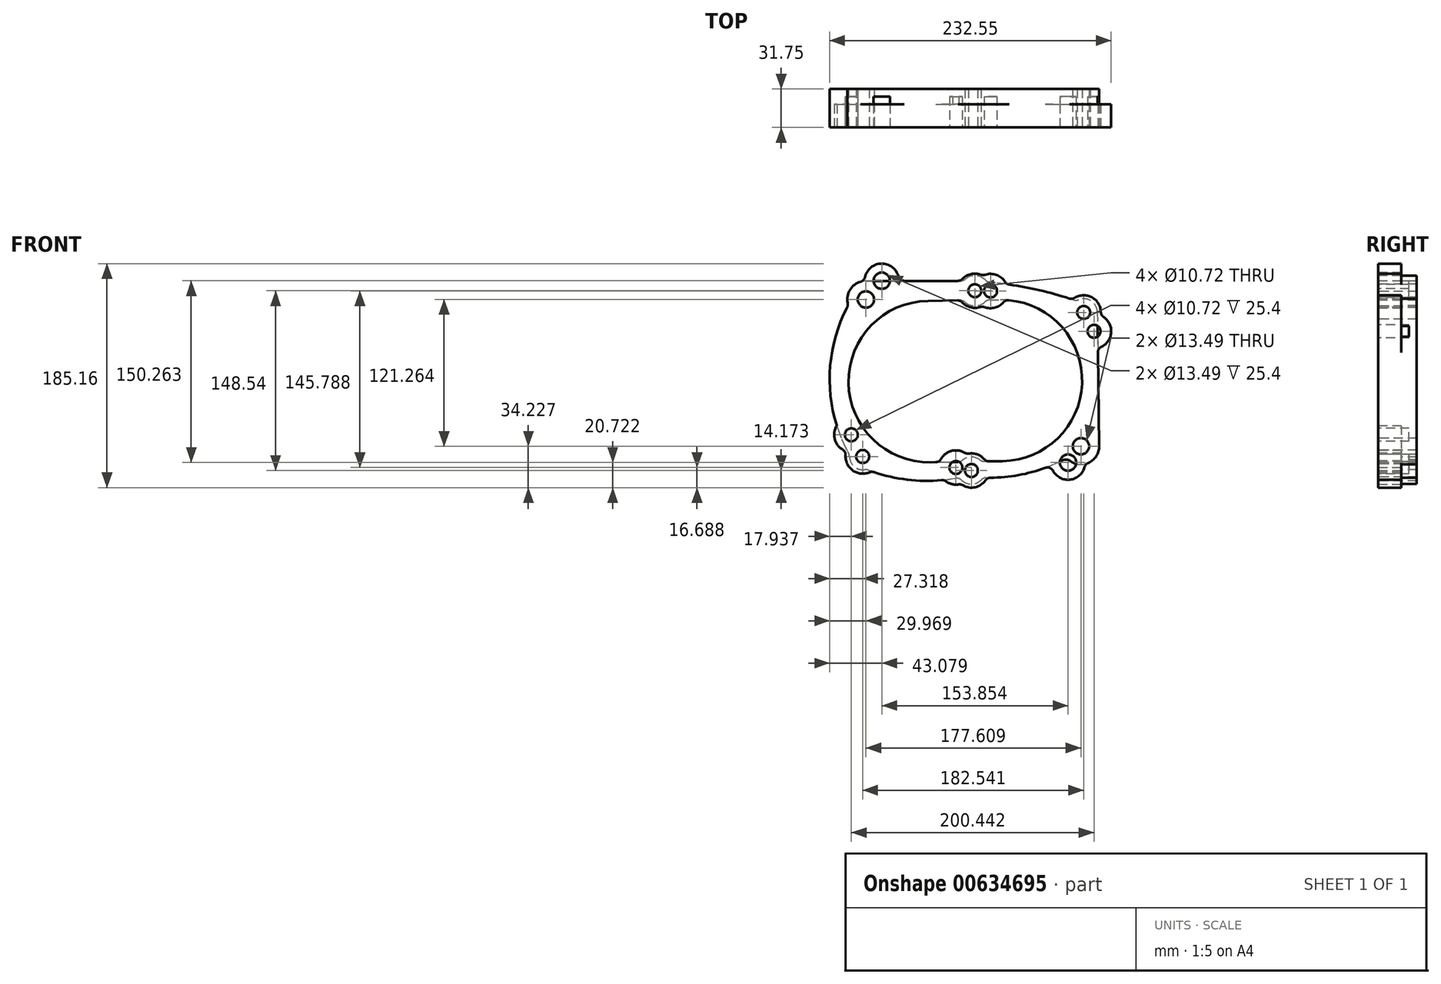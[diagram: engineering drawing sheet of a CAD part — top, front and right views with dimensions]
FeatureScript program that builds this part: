
annotation { "Feature Type Name" : "Feature", "Feature Type Description" : "" }
export const myFeature = defineFeature(function(context is Context, id is Id, definition is map)
    precondition{}
    {
        {
            var Q0;
            Q0=qCreatedBy(makeId("Front.planeOp"),FACE);
            var sketch = newSketch(context, id + "F0", { "sketchPlane" : qUnion([Q0])});
            skArc(sketch, "E0", {"start": v(18.49, 23.08) * mm, "mid": v(16.62, 24.35) * mm, "end": v(14.67, 25.49) * mm});
            skCircle(sketch, "E1", {"center": v(-15.7, 35.72) * mm, "radius": 1.38 * mm});
            skCircle(sketch, "E2", {"center": v(13.85, 35.93) * mm, "radius": 1.35 * mm});
            skCircle(sketch, "E3", {"center": v(20.07, 25.22) * mm, "radius": 1.06 * mm});
            skCircle(sketch, "E4", {"center": v(36, 22.94) * mm, "radius": 0.96 * mm});
            skCircle(sketch, "E5", {"center": v(32.47, 7.28) * mm, "radius": 1.06 * mm});
            skCircle(sketch, "E6", {"center": v(32.89, -9.33) * mm, "radius": 1.43 * mm});
            skCircle(sketch, "E7", {"center": v(29.86, -17.53) * mm, "radius": 1.14 * mm});
            skCircle(sketch, "E8", {"center": v(17.06, -30.92) * mm, "radius": 1 * mm});
            skCircle(sketch, "E9", {"center": v(-3.49, -35.34) * mm, "radius": 0.93 * mm});
            skCircle(sketch, "E10", {"center": v(-24.93, -24.43) * mm, "radius": 0.8 * mm});
            skCircle(sketch, "E11", {"center": v(-31.45, -13.73) * mm, "radius": 1.54 * mm});
            skCircle(sketch, "E12", {"center": v(-30.11, 13.1) * mm, "radius": 0.49 * mm});
            skArc(sketch, "E13", {"start": v(-33.12, -16.68) * mm, "mid": v(2.53, -38.1) * mm, "end": v(34.93, -12.05) * mm});
            skLineSegment(sketch, "E14", {"start": v(-10.28, -36.7) * mm, "end": v(-10.28, -31.1) * mm, "construction": true});
            skLineSegment(sketch, "E15", {"start": v(-6.15, -37.66) * mm, "end": v(-6.15, -32.24) * mm, "construction": true});
            skLineSegment(sketch, "E16", {"start": v(7.8, -37.36) * mm, "end": v(7.8, -31.88) * mm, "construction": true});
            skLineSegment(sketch, "E17", {"start": v(11.69, -36.28) * mm, "end": v(11.69, -30.6) * mm, "construction": true});
            skCircle(sketch, "E18", {"center": v(0.06, -1.86) * mm, "radius": 33.67 * mm, "construction": true});
            skLineSegment(sketch, "E19", {"start": v(0.06, 31.81) * mm, "end": v(0.06, 34.48) * mm, "construction": true});
            skLineSegment(sketch, "E20", {"start": v(0.06, 31.81) * mm, "end": v(0.06, 29.15) * mm, "construction": true});
            skArc(sketch, "E21", {"start": v(-34.65, -12.61) * mm, "mid": v(-34.62, -14.93) * mm, "end": v(-33.12, -16.68) * mm});
            skArc(sketch, "E22.trimOffspring", {"start": v(35.9, -7.76) * mm, "mid": v(36.4, -1.66) * mm, "end": v(35.84, 4.45) * mm});
            skArc(sketch, "E23.trimOffspring", {"start": v(34.93, -12.05) * mm, "mid": v(36.4, -10.13) * mm, "end": v(35.9, -7.76) * mm});
            skLineSegment(sketch, "E24", {"start": v(-18.74, 29.24) * mm, "end": v(-18.74, 35.72) * mm});
            skLineSegment(sketch, "E25", {"start": v(-15.7, 38.77) * mm, "end": v(13.85, 38.77) * mm});
            skLineSegment(sketch, "E26", {"start": v(16.69, 35.93) * mm, "end": v(16.69, 31.66) * mm});
            skArc(sketch, "E27.trimOffspring", {"start": v(-18.74, 29.24) * mm, "mid": v(-33.9, 11.05) * mm, "end": v(-34.65, -12.61) * mm});
            skArc(sketch, "E28", {"start": v(16.69, 31.66) * mm, "mid": v(17.37, 29.7) * mm, "end": v(19.11, 28.57) * mm});
            skArc(sketch, "E29", {"start": v(38.4, 22.45) * mm, "mid": v(37.98, 24.39) * mm, "end": v(36.27, 25.38) * mm});
            skArc(sketch, "E30", {"start": v(18.49, 23.08) * mm, "mid": v(20.67, 22.62) * mm, "end": v(22.44, 24) * mm});
            skArc(sketch, "E31", {"start": v(32.84, 9.91) * mm, "mid": v(30.46, 9.03) * mm, "end": v(29.9, 6.55) * mm});
            skLineSegment(sketch, "E32", {"start": v(19.11, 28.57) * mm, "end": v(36.63, 25.32) * mm});
            skLineSegment(sketch, "E33", {"start": v(38.4, 22.45) * mm, "end": v(35.84, 4.45) * mm});
            skArc(sketch, "E34", {"start": v(26.23, 26.04) * mm, "mid": v(24.02, 25.6) * mm, "end": v(22.44, 24) * mm});
            skArc(sketch, "E35.trimOffspring", {"start": v(35.67, 12.46) * mm, "mid": v(33.55, 21.05) * mm, "end": v(26.23, 26.04) * mm});
            skArc(sketch, "E36.trimOffspring", {"start": v(32.84, 9.91) * mm, "mid": v(34.73, 10.66) * mm, "end": v(35.67, 12.46) * mm});
            skArc(sketch, "E37.converted", {"start": v(-15.52, 32.68) * mm, "mid": v(-13.32, 33.82) * mm, "end": v(-12.69, 36.22) * mm});
            skArc(sketch, "E38.converted", {"start": v(11.03, 36.26) * mm, "mid": v(12.03, 33.76) * mm, "end": v(14.67, 33.22) * mm});
            skLineSegment(sketch, "E39", {"start": v(-15.52, 24.95) * mm, "end": v(-15.52, 32.68) * mm});
            skLineSegment(sketch, "E40", {"start": v(14.67, 25.49) * mm, "end": v(14.67, 33.22) * mm});
            skArc(sketch, "E41.trimOffspring", {"start": v(-15.52, 24.95) * mm, "mid": v(-11.58, -30.6) * mm, "end": v(29.9, 6.55) * mm});
            skLineSegment(sketch, "E42", {"start": v(-11.7, 37.38) * mm, "end": v(10.04, 37.38) * mm});
            skArc(sketch, "E43.trimOffspring", {"start": v(-15.7, 38.77) * mm, "mid": v(-17.85, 37.87) * mm, "end": v(-18.74, 35.72) * mm});
            skArc(sketch, "E44.trimOffspring", {"start": v(16.69, 35.93) * mm, "mid": v(15.86, 37.94) * mm, "end": v(13.85, 38.77) * mm});
            skArc(sketch, "E45", {"start": v(-11.7, 37.38) * mm, "mid": v(-12.47, 37.03) * mm, "end": v(-12.69, 36.22) * mm});
            skArc(sketch, "E46", {"start": v(11.03, 36.26) * mm, "mid": v(10.79, 37.04) * mm, "end": v(10.04, 37.38) * mm});
            skSolve(sketch);
        }
        {
            var Q0;
            Q0=qCreatedBy(makeId("Front.planeOp"),FACE);
            var sketch = newSketch(context, id + "F1", { "sketchPlane" : qUnion([Q0])});
            skCircle(sketch, "E47", {"center": v(145.83, 46.91) * mm, "radius": 5.36 * mm});
            skCircle(sketch, "E48", {"center": v(143.55, -63.66) * mm, "radius": 6.75 * mm});
            skCircle(sketch, "E49", {"center": v(53.04, -83.72) * mm, "radius": 5.36 * mm});
            skCircle(sketch, "E50", {"center": v(-36.71, -72.14) * mm, "radius": 5.36 * mm});
            skCircle(sketch, "E51", {"center": v(-34.06, 57.6) * mm, "radius": 6.75 * mm});
            skCircle(sketch, "E52", {"center": v(55.9, 64.82) * mm, "radius": 5.36 * mm});
            skSolve(sketch);
        }
        {
            var Q0;
            Q0=qCreatedBy(makeId("Front.planeOp"),FACE);
            var sketch = newSketch(context, id + "F2", { "sketchPlane" : qUnion([Q0])});
            skCircle(sketch, "E53.0", {"center": v(-34.06, 57.6) * mm, "radius": 6.75 * mm});
            skCircle(sketch, "E54.0", {"center": v(55.9, 64.82) * mm, "radius": 5.36 * mm});
            skCircle(sketch, "E55.0", {"center": v(145.83, 46.91) * mm, "radius": 5.36 * mm});
            skCircle(sketch, "E56.0", {"center": v(-36.71, -72.14) * mm, "radius": 5.36 * mm});
            skCircle(sketch, "E57.0", {"center": v(53.04, -83.72) * mm, "radius": 5.36 * mm});
            skCircle(sketch, "E58.0", {"center": v(143.55, -63.66) * mm, "radius": 6.75 * mm});
            skArc(sketch, "E59", {"start": v(-34.06, 72.97) * mm, "mid": v(-45.87, 67.43) * mm, "end": v(-49.17, 54.82) * mm});
            skArc(sketch, "E60", {"start": v(47.87, 55.34) * mm, "mid": v(56.08, 52.4) * mm, "end": v(64.2, 55.6) * mm});
            skArc(sketch, "E61", {"start": v(157.13, 47.06) * mm, "mid": v(152.12, 56.3) * mm, "end": v(141.68, 57.42) * mm});
            skArc(sketch, "E62", {"start": v(134.74, -75.88) * mm, "mid": v(150.5, -77.03) * mm, "end": v(158.61, -63.46) * mm});
            skArc(sketch, "E63", {"start": v(59.93, -74.87) * mm, "mid": v(52.87, -72.5) * mm, "end": v(45.89, -75.09) * mm});
            skArc(sketch, "E64", {"start": v(-47.62, -72.47) * mm, "mid": v(-43.8, -80.44) * mm, "end": v(-35.32, -82.97) * mm});
            skCircle(sketch, "E65", {"center": v(61.04, -9.57) * mm, "radius": 12.7 * mm});
            skLineSegment(sketch, "E66", {"start": v(61.04, -9.57) * mm, "end": v(53.04, -83.72) * mm, "construction": true});
            skLineSegment(sketch, "E67", {"start": v(55.9, 64.82) * mm, "end": v(61.04, -9.57) * mm, "construction": true});
            skLineSegment(sketch, "E68", {"start": v(-34.06, 57.6) * mm, "end": v(61.04, -9.57) * mm, "construction": true});
            skLineSegment(sketch, "E69", {"start": v(61.04, -9.57) * mm, "end": v(-36.71, -72.14) * mm, "construction": true});
            skLineSegment(sketch, "E70", {"start": v(61.04, -9.57) * mm, "end": v(145.83, 46.91) * mm, "construction": true});
            skLineSegment(sketch, "E71", {"start": v(61.04, -9.57) * mm, "end": v(143.55, -63.66) * mm, "construction": true});
            skLineSegment(sketch, "E72", {"start": v(-34.06, 72.97) * mm, "end": v(43.97, 72.97) * mm});
            skArc(sketch, "E73", {"start": v(137.34, 57.3) * mm, "mid": v(103.34, 66.54) * mm, "end": v(68.5, 71.84) * mm});
            skLineSegment(sketch, "E74", {"start": v(157.13, 47.06) * mm, "end": v(158.61, -63.46) * mm});
            skArc(sketch, "E75", {"start": v(-49.77, 50.77) * mm, "mid": v(-64.02, -9.6) * mm, "end": v(-48.39, -69.62) * mm});
            skArc(sketch, "E76", {"start": v(-32.26, -83.33) * mm, "mid": v(3.31, -91.62) * mm, "end": v(39.8, -90.16) * mm});
            skArc(sketch, "E77", {"start": v(65.67, -89.7) * mm, "mid": v(97.79, -86.34) * mm, "end": v(128.16, -75.37) * mm});
            skArc(sketch, "E78", {"start": v(78.86, -75.99) * mm, "mid": v(144.51, -8.3) * mm, "end": v(76.83, 57.35) * mm});
            skLineSegment(sketch, "E79", {"start": v(18.24, -10.22) * mm, "end": v(77.85, -9.32) * mm, "construction": true});
            skLineSegment(sketch, "E80", {"start": v(17.23, 56.44) * mm, "end": v(43.68, 56.85) * mm});
            skLineSegment(sketch, "E81", {"start": v(19.25, -76.89) * mm, "end": v(41.93, -76.55) * mm});
            skArc(sketch, "E82.trimOffspring", {"start": v(17.23, 56.44) * mm, "mid": v(-48.43, -11.23) * mm, "end": v(19.25, -76.89) * mm});
            skArc(sketch, "E83.trimOffspring", {"start": v(64.63, 73.65) * mm, "mid": v(56.46, 77.23) * mm, "end": v(48, 74.41) * mm});
            skLineSegment(sketch, "E84.trimOffspring", {"start": v(68.35, 57.22) * mm, "end": v(76.83, 57.35) * mm});
            skLineSegment(sketch, "E85.trimOffspring", {"start": v(63.93, -76.21) * mm, "end": v(78.86, -75.99) * mm});
            skArc(sketch, "E86.trimOffspring", {"start": v(45.3, -91.82) * mm, "mid": v(53.21, -94.93) * mm, "end": v(61.03, -91.59) * mm});
            skPoint(sketch, "E87.visualSharp", {"position": v(-48.67, 52.85) * mm});
            skArc(sketch, "E87.filletArc", {"start": v(-49.77, 50.77) * mm, "mid": v(-49.14, 52.74) * mm, "end": v(-49.17, 54.82) * mm});
            skPoint(sketch, "E88.visualSharp", {"position": v(-47.57, -71.1) * mm});
            skArc(sketch, "E88.filletArc", {"start": v(-47.62, -72.47) * mm, "mid": v(-47.84, -71) * mm, "end": v(-48.39, -69.62) * mm});
            skPoint(sketch, "E89.visualSharp", {"position": v(-33.91, -82.69) * mm});
            skArc(sketch, "E89.filletArc", {"start": v(-32.26, -83.33) * mm, "mid": v(-33.77, -82.96) * mm, "end": v(-35.32, -82.97) * mm});
            skPoint(sketch, "E90.visualSharp", {"position": v(43.42, -89.47) * mm});
            skArc(sketch, "E90.filletArc", {"start": v(45.3, -91.82) * mm, "mid": v(42.75, -90.33) * mm, "end": v(39.8, -90.16) * mm});
            skPoint(sketch, "E91.visualSharp", {"position": v(62.59, -89.6) * mm});
            skArc(sketch, "E91.filletArc", {"start": v(65.67, -89.7) * mm, "mid": v(63.15, -90.16) * mm, "end": v(61.03, -91.59) * mm});
            skPoint(sketch, "E92.visualSharp", {"position": v(44.46, -76.5) * mm});
            skArc(sketch, "E92.filletArc", {"start": v(41.93, -76.55) * mm, "mid": v(44.04, -76.15) * mm, "end": v(45.89, -75.09) * mm});
            skPoint(sketch, "E93.visualSharp", {"position": v(61.4, -76.25) * mm});
            skArc(sketch, "E93.filletArc", {"start": v(59.93, -74.87) * mm, "mid": v(61.82, -75.88) * mm, "end": v(63.93, -76.21) * mm});
            skPoint(sketch, "E94.visualSharp", {"position": v(132, -73.34) * mm});
            skArc(sketch, "E94.filletArc", {"start": v(134.74, -75.88) * mm, "mid": v(131.52, -74.7) * mm, "end": v(128.16, -75.37) * mm});
            skPoint(sketch, "E95.visualSharp", {"position": v(139.8, 56.47) * mm});
            skArc(sketch, "E95.filletArc", {"start": v(137.34, 57.3) * mm, "mid": v(139.52, 56.98) * mm, "end": v(141.68, 57.42) * mm});
            skPoint(sketch, "E96.visualSharp", {"position": v(65.68, 57.18) * mm});
            skArc(sketch, "E96.filletArc", {"start": v(68.35, 57.22) * mm, "mid": v(66.12, 56.78) * mm, "end": v(64.2, 55.6) * mm});
            skPoint(sketch, "E97.visualSharp", {"position": v(46.34, 56.89) * mm});
            skArc(sketch, "E97.filletArc", {"start": v(47.87, 55.34) * mm, "mid": v(45.91, 56.48) * mm, "end": v(43.68, 56.85) * mm});
            skPoint(sketch, "E98.visualSharp", {"position": v(46.52, 72.97) * mm});
            skArc(sketch, "E98.filletArc", {"start": v(43.97, 72.97) * mm, "mid": v(46.12, 73.34) * mm, "end": v(48, 74.41) * mm});
            skPoint(sketch, "E99.visualSharp", {"position": v(65.98, 72.06) * mm});
            skArc(sketch, "E99.filletArc", {"start": v(64.63, 73.65) * mm, "mid": v(66.4, 72.4) * mm, "end": v(68.5, 71.84) * mm});
            skSolve(sketch);
        }
        {
            var Q0;
            Q0=makeQuery(id+"F2.imprint","IMPRINT",FACE,{"disambiguationData":[TD([[makeQuery(id+"F2.imprint","IMPRINT",EDGE,{"derivedFrom":sQuery(id+"F2.wireOp",EDGE,"E53.0")}),-1.0]])]});
            extrude(context, id + "F3", {"entities" : qUnion([Q0]), "oppositeDirection" : true, "depth" : 12.7 * mm, "offsetDistance" : 25.4 * mm});
        }
        {
            var Q0;
            Q0=makeQuery(id+"F2.imprint","IMPRINT",FACE,{"disambiguationData":[TD([[makeQuery(id+"F2.imprint","IMPRINT",EDGE,{"derivedFrom":sQuery(id+"F2.wireOp",EDGE,"E53.0")}),-1.0]])]});
            extrude(context, id + "F4", {"entities" : qUnion([Q0]), "depth" : 19.05 * mm, "offsetDistance" : 25.4 * mm});
        }
        {
            var Q0;
            Q0=makeQuery(id+"F4.opExtrude","CAP_FACE",FACE,{"disambiguationData":[OSD([sQuery(id+"F2.wireOp",EDGE,"E53.0"),sQuery(id+"F2.wireOp",EDGE,"E54.0"),sQuery(id+"F2.wireOp",EDGE,"E55.0"),sQuery(id+"F2.wireOp",EDGE,"E56.0"),sQuery(id+"F2.wireOp",EDGE,"E57.0"),sQuery(id+"F2.wireOp",EDGE,"E58.0"),sQuery(id+"F2.wireOp",EDGE,"E59"),sQuery(id+"F2.wireOp",EDGE,"E60"),sQuery(id+"F2.wireOp",EDGE,"E61"),sQuery(id+"F2.wireOp",EDGE,"E62"),sQuery(id+"F2.wireOp",EDGE,"E63"),sQuery(id+"F2.wireOp",EDGE,"E64"),sQuery(id+"F2.wireOp",EDGE,"E72"),sQuery(id+"F2.wireOp",EDGE,"E73"),sQuery(id+"F2.wireOp",EDGE,"E74"),sQuery(id+"F2.wireOp",EDGE,"E75"),sQuery(id+"F2.wireOp",EDGE,"E76"),sQuery(id+"F2.wireOp",EDGE,"E77"),sQuery(id+"F2.wireOp",EDGE,"E78"),sQuery(id+"F2.wireOp",EDGE,"E80"),sQuery(id+"F2.wireOp",EDGE,"E81"),sQuery(id+"F2.wireOp",EDGE,"E82.trimOffspring"),sQuery(id+"F2.wireOp",EDGE,"E83.trimOffspring"),sQuery(id+"F2.wireOp",EDGE,"E84.trimOffspring"),sQuery(id+"F2.wireOp",EDGE,"E85.trimOffspring"),sQuery(id+"F2.wireOp",EDGE,"E86.trimOffspring"),sQuery(id+"F2.wireOp",EDGE,"E87.filletArc"),sQuery(id+"F2.wireOp",EDGE,"E88.filletArc"),sQuery(id+"F2.wireOp",EDGE,"E89.filletArc"),sQuery(id+"F2.wireOp",EDGE,"E90.filletArc"),sQuery(id+"F2.wireOp",EDGE,"E91.filletArc"),sQuery(id+"F2.wireOp",EDGE,"E92.filletArc"),sQuery(id+"F2.wireOp",EDGE,"E93.filletArc"),sQuery(id+"F2.wireOp",EDGE,"E94.filletArc"),sQuery(id+"F2.wireOp",EDGE,"E95.filletArc"),sQuery(id+"F2.wireOp",EDGE,"E96.filletArc"),sQuery(id+"F2.wireOp",EDGE,"E97.filletArc"),sQuery(id+"F2.wireOp",EDGE,"E98.filletArc"),sQuery(id+"F2.wireOp",EDGE,"E99.filletArc")])],"isStart":false});
            var sketch = newSketch(context, id + "F5", { "sketchPlane" : qUnion([Q0])});
            skCircle(sketch, "E100.0", {"center": v(-34.06, 57.6) * mm, "radius": 6.75 * mm});
            skCircle(sketch, "E101.0", {"center": v(55.9, 64.82) * mm, "radius": 5.36 * mm});
            skCircle(sketch, "E102.0", {"center": v(145.83, 46.91) * mm, "radius": 5.36 * mm});
            skCircle(sketch, "E103.0", {"center": v(143.55, -63.66) * mm, "radius": 6.75 * mm});
            skCircle(sketch, "E104.0", {"center": v(53.04, -83.72) * mm, "radius": 5.36 * mm});
            skCircle(sketch, "E105.0", {"center": v(-36.71, -72.14) * mm, "radius": 5.36 * mm});
            skCircle(sketch, "E106.0", {"center": v(61.04, -9.57) * mm, "radius": 12.7 * mm});
            skCircle(sketch, "E107.1.0", {"center": v(-20.95, 73.1) * mm, "radius": 6.75 * mm});
            skCircle(sketch, "E107.1.1", {"center": v(68.89, 64.59) * mm, "radius": 5.36 * mm});
            skCircle(sketch, "E107.1.2", {"center": v(154.35, 31.33) * mm, "radius": 5.36 * mm});
            skCircle(sketch, "E107.1.3", {"center": v(132.9, -77.17) * mm, "radius": 6.75 * mm});
            skCircle(sketch, "E107.1.4", {"center": v(40.3, -81.2) * mm, "radius": 5.36 * mm});
            skCircle(sketch, "E107.1.5", {"center": v(-46.1, -54.22) * mm, "radius": 5.36 * mm});
            skLineSegment(sketch, "E107.anchor1", {"start": v(61.04, -9.57) * mm, "end": v(-34.06, 57.6) * mm, "construction": true});
            skLineSegment(sketch, "E107.anchor2", {"start": v(61.04, -9.57) * mm, "end": v(-20.95, 73.1) * mm, "construction": true});
            skCircle(sketch, "E108", {"center": v(68.89, 64.59) * mm, "radius": 14.17 * mm});
            skCircle(sketch, "E109", {"center": v(154.35, 31.33) * mm, "radius": 14.17 * mm});
            skCircle(sketch, "E110", {"center": v(132.9, -77.17) * mm, "radius": 14.17 * mm});
            skCircle(sketch, "E111", {"center": v(40.3, -81.2) * mm, "radius": 14.17 * mm});
            skCircle(sketch, "E112", {"center": v(-46.1, -54.22) * mm, "radius": 14.17 * mm});
            skCircle(sketch, "E113", {"center": v(-20.95, 73.1) * mm, "radius": 14.17 * mm});
            skCircle(sketch, "E114.cCircle", {"center": v(-20.95, 73.1) * mm, "radius": 9.53 * mm, "construction": true});
            skLineSegment(sketch, "E114.0", {"start": v(-16.08, 82.96) * mm, "end": v(-9.98, 73.8) * mm, "construction": true});
            skLineSegment(sketch, "E114.1", {"start": v(-9.98, 73.8) * mm, "end": v(-14.85, 63.95) * mm, "construction": true});
            skLineSegment(sketch, "E114.2", {"start": v(-14.85, 63.95) * mm, "end": v(-25.82, 63.23) * mm, "construction": true});
            skLineSegment(sketch, "E114.3", {"start": v(-25.82, 63.23) * mm, "end": v(-31.93, 72.38) * mm, "construction": true});
            skLineSegment(sketch, "E114.4", {"start": v(-31.93, 72.38) * mm, "end": v(-27.05, 82.24) * mm, "construction": true});
            skLineSegment(sketch, "E114.5", {"start": v(-27.05, 82.24) * mm, "end": v(-16.08, 82.96) * mm, "construction": true});
            skPoint(sketch, "E114.0.midPoint", {"position": v(-13.03, 78.38) * mm});
            skLineSegment(sketch, "E115.0", {"start": v(-27.22, 82.49) * mm, "end": v(-15.95, 83.22) * mm, "construction": true});
            skLineSegment(sketch, "E115.1", {"start": v(-9.68, 73.82) * mm, "end": v(-14.69, 63.7) * mm, "construction": true});
            skLineSegment(sketch, "E115.2", {"start": v(-14.69, 63.7) * mm, "end": v(-25.95, 62.97) * mm, "construction": true});
            skLineSegment(sketch, "E115.3", {"start": v(-15.95, 83.22) * mm, "end": v(-9.68, 73.82) * mm, "construction": true});
            skLineSegment(sketch, "E115.4", {"start": v(-25.95, 62.97) * mm, "end": v(-32.22, 72.36) * mm, "construction": true});
            skLineSegment(sketch, "E115.5", {"start": v(-32.22, 72.36) * mm, "end": v(-27.22, 82.49) * mm, "construction": true});
            skCircle(sketch, "E116", {"center": v(55.9, 64.82) * mm, "radius": 14.17 * mm});
            skCircle(sketch, "E117", {"center": v(145.83, 46.91) * mm, "radius": 14.17 * mm});
            skCircle(sketch, "E118", {"center": v(143.55, -63.66) * mm, "radius": 14.17 * mm, "construction": true});
            skCircle(sketch, "E119", {"center": v(53.04, -83.72) * mm, "radius": 14.17 * mm});
            skCircle(sketch, "E120", {"center": v(-36.71, -72.14) * mm, "radius": 14.17 * mm});
            skCircle(sketch, "E121", {"center": v(-34.06, 57.6) * mm, "radius": 14.17 * mm, "construction": true});
            skCircle(sketch, "E122", {"center": v(55.9, 64.82) * mm, "radius": 6.35 * mm, "construction": true});
            skCircle(sketch, "E123", {"center": v(68.89, 64.59) * mm, "radius": 6.35 * mm, "construction": true});
            skCircle(sketch, "E124", {"center": v(143.55, -63.66) * mm, "radius": 7.94 * mm, "construction": true});
            skCircle(sketch, "E125", {"center": v(132.9, -77.17) * mm, "radius": 7.94 * mm, "construction": true});
            skSolve(sketch);
        }
        {
            var Q0;
            {var subQ0=makeQuery(id+"F4.opExtrude","CAP_EDGE",EDGE,{"disambiguationData":[OSD([sQuery(id+"F2.wireOp",EDGE,"E72")])],"isStart":false});var subQ3=sQuery(id+"F5.wireOp",EDGE,"E107.1.0");var subQ4=makeQuery(id+"F5.imprint","INTERSECT",VERTEX,{"disambiguationData":[OD(0.0)],"derivedFrom":[subQ0,subQ3]});Q0=makeQuery(id+"F5.imprint","IMPRINT",FACE,{"disambiguationData":[TD([[makeQuery(id+"F5.imprint","IMPRINT",EDGE,{"disambiguationData":[TD([[subQ4,1.0]])],"derivedFrom":subQ3}),-1.0]])]});}
            var Q1;
            {var subQ5=makeQuery(id+"F4.opExtrude","CAP_EDGE",EDGE,{"disambiguationData":[OSD([sQuery(id+"F2.wireOp",EDGE,"E99.filletArc")])],"isStart":false});Q1=makeQuery(id+"F5.imprint","IMPRINT",FACE,{"disambiguationData":[TD([[makeQuery(id+"F5.imprint","IMPRINT",EDGE,{"derivedFrom":subQ5}),1.0]])]});}
            var Q2;
            {var subQ4=makeQuery(id+"F4.opExtrude","CAP_EDGE",EDGE,{"disambiguationData":[OSD([sQuery(id+"F2.wireOp",EDGE,"E84.trimOffspring")])],"isStart":false});Q2=makeQuery(id+"F5.imprint","IMPRINT",FACE,{"disambiguationData":[TD([[makeQuery(id+"F5.imprint","IMPRINT",EDGE,{"derivedFrom":subQ4}),-1.0]])]});}
            var Q3;
            {var subQ0=sQuery(id+"F5.wireOp",EDGE,"E107.1.2");var subQ1=makeQuery(id+"F4.opExtrude","CAP_EDGE",EDGE,{"disambiguationData":[OSD([sQuery(id+"F2.wireOp",EDGE,"E74")])],"isStart":false});var subQ2=makeQuery(id+"F5.imprint","INTERSECT",VERTEX,{"disambiguationData":[OD(0.0)],"derivedFrom":[subQ1,subQ0]});Q3=makeQuery(id+"F5.imprint","IMPRINT",FACE,{"disambiguationData":[TD([[makeQuery(id+"F5.imprint","IMPRINT",EDGE,{"disambiguationData":[TD([[subQ2,1.0]])],"derivedFrom":subQ0}),-1.0]])]});}
            var Q4;
            {var subQ0=sQuery(id+"F5.wireOp",EDGE,"E107.1.3");var subQ1=makeQuery(id+"F4.opExtrude","CAP_EDGE",EDGE,{"disambiguationData":[OSD([sQuery(id+"F2.wireOp",EDGE,"E62")])],"isStart":false});var subQ2=makeQuery(id+"F5.imprint","INTERSECT",VERTEX,{"derivedFrom":[subQ1,subQ0]});Q4=makeQuery(id+"F5.imprint","IMPRINT",FACE,{"disambiguationData":[TD([[makeQuery(id+"F5.imprint","IMPRINT",EDGE,{"disambiguationData":[TD([[subQ2,1.0]])],"derivedFrom":subQ0}),-1.0]])]});}
            var Q5;
            {var subQ5=makeQuery(id+"F4.opExtrude","CAP_EDGE",EDGE,{"disambiguationData":[OSD([sQuery(id+"F2.wireOp",EDGE,"E90.filletArc")])],"isStart":false});Q5=makeQuery(id+"F5.imprint","IMPRINT",FACE,{"disambiguationData":[TD([[makeQuery(id+"F5.imprint","IMPRINT",EDGE,{"derivedFrom":subQ5}),1.0]])]});}
            var Q6;
            {var subQ1=makeQuery(id+"F4.opExtrude","CAP_EDGE",EDGE,{"disambiguationData":[OSD([sQuery(id+"F2.wireOp",EDGE,"E81")])],"isStart":false});var subQ3=sQuery(id+"F5.wireOp",EDGE,"E107.1.4");var subQ4=makeQuery(id+"F5.imprint","INTERSECT",VERTEX,{"derivedFrom":[subQ1,subQ3]});Q6=makeQuery(id+"F5.imprint","IMPRINT",FACE,{"disambiguationData":[TD([[makeQuery(id+"F5.imprint","IMPRINT",EDGE,{"disambiguationData":[TD([[subQ4,1.0]])],"derivedFrom":subQ3}),-1.0]])]});}
            var Q7;
            {var subQ0=sQuery(id+"F5.wireOp",EDGE,"E112");var subQ1=makeQuery(id+"F4.opExtrude","CAP_EDGE",EDGE,{"disambiguationData":[OSD([sQuery(id+"F2.wireOp",EDGE,"E82.trimOffspring")])],"isStart":false});var subQ2=makeQuery(id+"F5.imprint","INTERSECT",VERTEX,{"disambiguationData":[OD(0.0)],"derivedFrom":[subQ1,subQ0]});Q7=makeQuery(id+"F5.imprint","IMPRINT",FACE,{"disambiguationData":[TD([[makeQuery(id+"F5.imprint","IMPRINT",EDGE,{"disambiguationData":[TD([[subQ2,1.0]])],"derivedFrom":subQ0}),1.0]])]});}
            var Q8;
            {var subQ0=sQuery(id+"F5.wireOp",EDGE,"E112");var subQ1=makeQuery(id+"F4.opExtrude","CAP_EDGE",EDGE,{"disambiguationData":[OSD([sQuery(id+"F2.wireOp",EDGE,"E75")])],"isStart":false});var subQ2=makeQuery(id+"F5.imprint","INTERSECT",VERTEX,{"disambiguationData":[OD(0.0)],"derivedFrom":[subQ1,subQ0]});Q8=makeQuery(id+"F5.imprint","IMPRINT",FACE,{"disambiguationData":[TD([[makeQuery(id+"F5.imprint","IMPRINT",EDGE,{"disambiguationData":[TD([[subQ2,-1.0]])],"derivedFrom":subQ0}),1.0]])]});}
            var Q9;
            {var subQ0=sQuery(id+"F5.wireOp",EDGE,"E113");var subQ1=makeQuery(id+"F4.opExtrude","CAP_EDGE",EDGE,{"disambiguationData":[OSD([sQuery(id+"F2.wireOp",EDGE,"E59")])],"isStart":false});var subQ2=makeQuery(id+"F5.imprint","INTERSECT",VERTEX,{"derivedFrom":[subQ1,subQ0]});Q9=makeQuery(id+"F5.imprint","IMPRINT",FACE,{"disambiguationData":[TD([[makeQuery(id+"F5.imprint","IMPRINT",EDGE,{"disambiguationData":[TD([[subQ2,1.0]])],"derivedFrom":subQ0}),1.0]])]});}
            var Q10;
            {var subQ0=sQuery(id+"F5.wireOp",EDGE,"E116");var subQ1=sQuery(id+"F5.wireOp",EDGE,"E108");var subQ2=makeQuery(id+"F5.imprint","INTERSECT",VERTEX,{"disambiguationData":[OD(0.0)],"derivedFrom":[subQ1,subQ0]});Q10=makeQuery(id+"F5.imprint","IMPRINT",FACE,{"disambiguationData":[TD([[makeQuery(id+"F5.imprint","IMPRINT",EDGE,{"disambiguationData":[TD([[subQ2,-1.0]])],"derivedFrom":subQ1}),-1.0]])]});}
            var Q11;
            {var subQ0=sQuery(id+"F5.wireOp",EDGE,"E116");var subQ1=sQuery(id+"F5.wireOp",EDGE,"E108");var subQ2=makeQuery(id+"F5.imprint","INTERSECT",VERTEX,{"disambiguationData":[OD(1.0)],"derivedFrom":[subQ1,subQ0]});Q11=makeQuery(id+"F5.imprint","IMPRINT",FACE,{"disambiguationData":[TD([[makeQuery(id+"F5.imprint","IMPRINT",EDGE,{"disambiguationData":[TD([[subQ2,1.0]])],"derivedFrom":subQ1}),-1.0]])]});}
            var Q12;
            {var subQ0=sQuery(id+"F5.wireOp",EDGE,"E116");var subQ1=sQuery(id+"F5.wireOp",EDGE,"E108");var subQ2=makeQuery(id+"F5.imprint","INTERSECT",VERTEX,{"disambiguationData":[OD(1.0)],"derivedFrom":[subQ1,subQ0]});Q12=makeQuery(id+"F5.imprint","IMPRINT",FACE,{"disambiguationData":[TD([[makeQuery(id+"F5.imprint","IMPRINT",EDGE,{"disambiguationData":[TD([[subQ2,1.0]])],"derivedFrom":subQ1}),1.0]])]});}
            var Q13;
            {var subQ1=makeQuery(id+"F4.opExtrude","CAP_EDGE",EDGE,{"disambiguationData":[OSD([sQuery(id+"F2.wireOp",EDGE,"E61")])],"isStart":false});Q13=makeQuery(id+"F5.imprint","IMPRINT",FACE,{"disambiguationData":[TD([[makeQuery(id+"F5.imprint","IMPRINT",EDGE,{"derivedFrom":subQ1}),-1.0]])]});}
            var Q14;
            {var subQ0=sQuery(id+"F5.wireOp",EDGE,"E117");var subQ1=sQuery(id+"F5.wireOp",EDGE,"E109");var subQ2=makeQuery(id+"F5.imprint","INTERSECT",VERTEX,{"disambiguationData":[OD(0.0)],"derivedFrom":[subQ1,subQ0]});Q14=makeQuery(id+"F5.imprint","IMPRINT",FACE,{"disambiguationData":[TD([[makeQuery(id+"F5.imprint","IMPRINT",EDGE,{"disambiguationData":[TD([[subQ2,-1.0]])],"derivedFrom":subQ1}),1.0]])]});}
            var Q15;
            {var subQ5=sQuery(id+"F5.wireOp",EDGE,"E119");var subQ7=sQuery(id+"F5.wireOp",EDGE,"E107.1.4");var subQ8=makeQuery(id+"F5.imprint","INTERSECT",VERTEX,{"disambiguationData":[OD(0.0)],"derivedFrom":[subQ7,subQ5]});Q15=makeQuery(id+"F5.imprint","IMPRINT",FACE,{"disambiguationData":[TD([[makeQuery(id+"F5.imprint","IMPRINT",EDGE,{"disambiguationData":[TD([[subQ8,1.0]])],"derivedFrom":subQ7}),-1.0]])]});}
            var Q16;
            {var subQ5=makeQuery(id+"F4.opExtrude","CAP_EDGE",EDGE,{"disambiguationData":[OSD([sQuery(id+"F2.wireOp",EDGE,"E93.filletArc")])],"isStart":false});Q16=makeQuery(id+"F5.imprint","IMPRINT",FACE,{"disambiguationData":[TD([[makeQuery(id+"F5.imprint","IMPRINT",EDGE,{"derivedFrom":subQ5}),1.0]])]});}
            var Q17;
            {var subQ0=makeQuery(id+"F4.opExtrude","CAP_EDGE",EDGE,{"disambiguationData":[OSD([sQuery(id+"F2.wireOp",EDGE,"E91.filletArc")])],"isStart":false});Q17=makeQuery(id+"F5.imprint","IMPRINT",FACE,{"disambiguationData":[TD([[makeQuery(id+"F5.imprint","IMPRINT",EDGE,{"derivedFrom":subQ0}),1.0]])]});}
            var Q18;
            {var subQ0=sQuery(id+"F5.wireOp",EDGE,"E120");var subQ1=sQuery(id+"F5.wireOp",EDGE,"E112");var subQ2=makeQuery(id+"F5.imprint","INTERSECT",VERTEX,{"disambiguationData":[OD(0.0)],"derivedFrom":[subQ1,subQ0]});Q18=makeQuery(id+"F5.imprint","IMPRINT",FACE,{"disambiguationData":[TD([[makeQuery(id+"F5.imprint","IMPRINT",EDGE,{"disambiguationData":[TD([[subQ2,-1.0]])],"derivedFrom":subQ1}),1.0]])]});}
            var Q19;
            Q19=makeQuery(id+"F5.imprint","IMPRINT",FACE,{"disambiguationData":[TD([[makeQuery(id+"F5.imprint","IMPRINT",EDGE,{"derivedFrom":makeQuery(id+"F4.opExtrude","CAP_EDGE",EDGE,{"disambiguationData":[OSD([sQuery(id+"F2.wireOp",EDGE,"E64")])],"isStart":false})}),-1.0]])]});
            var Q20;
            Q20=makeQuery(id+"F4.opExtrude","CAP_FACE",FACE,{"disambiguationData":[OSD([sQuery(id+"F2.wireOp",EDGE,"E53.0"),sQuery(id+"F2.wireOp",EDGE,"E54.0"),sQuery(id+"F2.wireOp",EDGE,"E55.0"),sQuery(id+"F2.wireOp",EDGE,"E56.0"),sQuery(id+"F2.wireOp",EDGE,"E57.0"),sQuery(id+"F2.wireOp",EDGE,"E58.0"),sQuery(id+"F2.wireOp",EDGE,"E59"),sQuery(id+"F2.wireOp",EDGE,"E60"),sQuery(id+"F2.wireOp",EDGE,"E61"),sQuery(id+"F2.wireOp",EDGE,"E62"),sQuery(id+"F2.wireOp",EDGE,"E63"),sQuery(id+"F2.wireOp",EDGE,"E64"),sQuery(id+"F2.wireOp",EDGE,"E72"),sQuery(id+"F2.wireOp",EDGE,"E73"),sQuery(id+"F2.wireOp",EDGE,"E74"),sQuery(id+"F2.wireOp",EDGE,"E75"),sQuery(id+"F2.wireOp",EDGE,"E76"),sQuery(id+"F2.wireOp",EDGE,"E77"),sQuery(id+"F2.wireOp",EDGE,"E78"),sQuery(id+"F2.wireOp",EDGE,"E80"),sQuery(id+"F2.wireOp",EDGE,"E81"),sQuery(id+"F2.wireOp",EDGE,"E82.trimOffspring"),sQuery(id+"F2.wireOp",EDGE,"E83.trimOffspring"),sQuery(id+"F2.wireOp",EDGE,"E84.trimOffspring"),sQuery(id+"F2.wireOp",EDGE,"E85.trimOffspring"),sQuery(id+"F2.wireOp",EDGE,"E86.trimOffspring"),sQuery(id+"F2.wireOp",EDGE,"E87.filletArc"),sQuery(id+"F2.wireOp",EDGE,"E88.filletArc"),sQuery(id+"F2.wireOp",EDGE,"E89.filletArc"),sQuery(id+"F2.wireOp",EDGE,"E90.filletArc"),sQuery(id+"F2.wireOp",EDGE,"E91.filletArc"),sQuery(id+"F2.wireOp",EDGE,"E92.filletArc"),sQuery(id+"F2.wireOp",EDGE,"E93.filletArc"),sQuery(id+"F2.wireOp",EDGE,"E94.filletArc"),sQuery(id+"F2.wireOp",EDGE,"E95.filletArc"),sQuery(id+"F2.wireOp",EDGE,"E96.filletArc"),sQuery(id+"F2.wireOp",EDGE,"E97.filletArc"),sQuery(id+"F2.wireOp",EDGE,"E98.filletArc"),sQuery(id+"F2.wireOp",EDGE,"E99.filletArc")])],"isStart":true});
            extrude(context, id + "F6", {"entities" : qUnion([Q0, Q1, Q2, Q3, Q4, Q5, Q6, Q7, Q8, Q9, Q10, Q11, Q12, Q13, Q14, Q15, Q16, Q17, Q18, Q19]), "operationType" : NewBodyOperationType.ADD, "endBound" : BoundingType.UP_TO_SURFACE, "oppositeDirection" : true, "depth" : 25.4 * mm, "endBoundEntityFace" : qUnion([Q20]), "offsetDistance" : 25.4 * mm});
        }
        {
            var Q0;
            {var subQ0=sQuery(id+"F5.wireOp",EDGE,"E120");var subQ1=sQuery(id+"F5.wireOp",EDGE,"E107.1.5");var subQ2=makeQuery(id+"F5.imprint","INTERSECT",VERTEX,{"disambiguationData":[OD(0.0)],"derivedFrom":[subQ1,subQ0]});Q0=makeQuery(id+"F5.imprint","IMPRINT",FACE,{"disambiguationData":[TD([[makeQuery(id+"F5.imprint","IMPRINT",EDGE,{"disambiguationData":[TD([[subQ2,-1.0]])],"derivedFrom":subQ1}),1.0]])]});}
            var Q1;
            {var subQ0=sQuery(id+"F5.wireOp",EDGE,"E116");var subQ1=sQuery(id+"F5.wireOp",EDGE,"E107.1.1");var subQ2=makeQuery(id+"F5.imprint","INTERSECT",VERTEX,{"disambiguationData":[OD(0.0)],"derivedFrom":[subQ1,subQ0]});Q1=makeQuery(id+"F5.imprint","IMPRINT",FACE,{"disambiguationData":[TD([[makeQuery(id+"F5.imprint","IMPRINT",EDGE,{"disambiguationData":[TD([[subQ2,-1.0]])],"derivedFrom":subQ1}),1.0]])]});}
            var Q2;
            {var subQ0=sQuery(id+"F5.wireOp",EDGE,"E116");var subQ1=sQuery(id+"F5.wireOp",EDGE,"E107.1.1");var subQ2=makeQuery(id+"F5.imprint","INTERSECT",VERTEX,{"disambiguationData":[OD(0.0)],"derivedFrom":[subQ1,subQ0]});Q2=makeQuery(id+"F5.imprint","IMPRINT",FACE,{"disambiguationData":[TD([[makeQuery(id+"F5.imprint","IMPRINT",EDGE,{"disambiguationData":[TD([[subQ2,1.0]])],"derivedFrom":subQ1}),1.0]])]});}
            var Q3;
            {var subQ0=sQuery(id+"F5.wireOp",EDGE,"E117");var subQ1=sQuery(id+"F5.wireOp",EDGE,"E107.1.2");var subQ2=makeQuery(id+"F5.imprint","INTERSECT",VERTEX,{"disambiguationData":[OD(0.0)],"derivedFrom":[subQ1,subQ0]});Q3=makeQuery(id+"F5.imprint","IMPRINT",FACE,{"disambiguationData":[TD([[makeQuery(id+"F5.imprint","IMPRINT",EDGE,{"disambiguationData":[TD([[subQ2,1.0]])],"derivedFrom":subQ1}),1.0]])]});}
            var Q4;
            {var subQ5=makeQuery(id+"F4.opExtrude","CAP_EDGE",EDGE,{"disambiguationData":[OSD([sQuery(id+"F2.wireOp",EDGE,"E94.filletArc")])],"isStart":false});Q4=makeQuery(id+"F5.imprint","IMPRINT",FACE,{"disambiguationData":[TD([[makeQuery(id+"F5.imprint","IMPRINT",EDGE,{"derivedFrom":subQ5}),-1.0]])]});}
            var Q5;
            {var subQ0=sQuery(id+"F5.wireOp",EDGE,"E119");var subQ1=sQuery(id+"F5.wireOp",EDGE,"E107.1.4");var subQ2=makeQuery(id+"F5.imprint","INTERSECT",VERTEX,{"disambiguationData":[OD(1.0)],"derivedFrom":[subQ1,subQ0]});Q5=makeQuery(id+"F5.imprint","IMPRINT",FACE,{"disambiguationData":[TD([[makeQuery(id+"F5.imprint","IMPRINT",EDGE,{"disambiguationData":[TD([[subQ2,1.0]])],"derivedFrom":subQ1}),1.0]])]});}
            var Q6;
            {var subQ0=sQuery(id+"F5.wireOp",EDGE,"E107.1.0");var subQ1=makeQuery(id+"F4.opExtrude","CAP_EDGE",EDGE,{"disambiguationData":[OSD([sQuery(id+"F2.wireOp",EDGE,"E72")])],"isStart":false});var subQ2=makeQuery(id+"F5.imprint","INTERSECT",VERTEX,{"disambiguationData":[OD(0.0)],"derivedFrom":[subQ1,subQ0]});Q6=makeQuery(id+"F5.imprint","IMPRINT",FACE,{"disambiguationData":[TD([[makeQuery(id+"F5.imprint","IMPRINT",EDGE,{"disambiguationData":[TD([[subQ2,-1.0]])],"derivedFrom":subQ0}),1.0]])]});}
            var Q7;
            {var subQ0=sQuery(id+"F5.wireOp",EDGE,"E120");var subQ1=sQuery(id+"F5.wireOp",EDGE,"E107.1.5");var subQ2=makeQuery(id+"F5.imprint","INTERSECT",VERTEX,{"disambiguationData":[OD(0.0)],"derivedFrom":[subQ1,subQ0]});Q7=makeQuery(id+"F5.imprint","IMPRINT",FACE,{"disambiguationData":[TD([[makeQuery(id+"F5.imprint","IMPRINT",EDGE,{"disambiguationData":[TD([[subQ2,1.0]])],"derivedFrom":subQ1}),1.0]])]});}
            var Q8;
            {var subQ0=sQuery(id+"F5.wireOp",EDGE,"E119");var subQ1=sQuery(id+"F5.wireOp",EDGE,"E107.1.4");var subQ2=makeQuery(id+"F5.imprint","INTERSECT",VERTEX,{"disambiguationData":[OD(1.0)],"derivedFrom":[subQ1,subQ0]});Q8=makeQuery(id+"F5.imprint","IMPRINT",FACE,{"disambiguationData":[TD([[makeQuery(id+"F5.imprint","IMPRINT",EDGE,{"disambiguationData":[TD([[subQ2,-1.0]])],"derivedFrom":subQ1}),1.0]])]});}
            var Q9;
            {var subQ0=sQuery(id+"F5.wireOp",EDGE,"E117");var subQ1=sQuery(id+"F5.wireOp",EDGE,"E107.1.2");var subQ2=makeQuery(id+"F5.imprint","INTERSECT",VERTEX,{"disambiguationData":[OD(0.0)],"derivedFrom":[subQ1,subQ0]});Q9=makeQuery(id+"F5.imprint","IMPRINT",FACE,{"disambiguationData":[TD([[makeQuery(id+"F5.imprint","IMPRINT",EDGE,{"disambiguationData":[TD([[subQ2,-1.0]])],"derivedFrom":subQ1}),1.0]])]});}
            extrude(context, id + "F7", {"entities" : qUnion([Q0, Q1, Q2, Q3, Q4, Q5, Q6, Q7, Q8, Q9]), "operationType" : NewBodyOperationType.REMOVE, "oppositeDirection" : true, "depth" : 25.4 * mm, "offsetDistance" : 25.4 * mm});
        }
        {
            var Q0;
            Q0=makeQuery(id+"F6.opExtrude","SWEPT_EDGE",EDGE,{"disambiguationData":[OSD([sQuery(id+"F2.wireOp",EDGE,"E73"),sQuery(id+"F5.wireOp",EDGE,"E117")])]});
            var Q1;
            Q1=makeQuery(id+"F6.opExtrude","SWEPT_EDGE",EDGE,{"disambiguationData":[OSD([sQuery(id+"F5.wireOp",EDGE,"E109"),sQuery(id+"F5.wireOp",EDGE,"E117")])]});
            var Q2;
            Q2=makeQuery(id+"F6.opExtrude","SWEPT_EDGE",EDGE,{"disambiguationData":[OSD([sQuery(id+"F2.wireOp",EDGE,"E74"),sQuery(id+"F5.wireOp",EDGE,"E109")])]});
            var Q3;
            Q3=makeQuery(id+"F6.opExtrude","SWEPT_EDGE",EDGE,{"disambiguationData":[OSD([sQuery(id+"F2.wireOp",EDGE,"E62"),sQuery(id+"F5.wireOp",EDGE,"E110")])]});
            var Q4;
            Q4=makeQuery(id+"F6.opExtrude","SWEPT_EDGE",EDGE,{"disambiguationData":[OSD([sQuery(id+"F2.wireOp",EDGE,"E77"),sQuery(id+"F5.wireOp",EDGE,"E110")])]});
            var Q5;
            Q5=makeQuery(id+"F6.opExtrude","SWEPT_EDGE",EDGE,{"disambiguationData":[OSD([sQuery(id+"F2.wireOp",EDGE,"E77"),sQuery(id+"F5.wireOp",EDGE,"E119")])]});
            var Q6;
            {var subQ0=sQuery(id+"F5.wireOp",EDGE,"E119");var subQ1=sQuery(id+"F5.wireOp",EDGE,"E111");Q6=makeQuery(id+"F6.opExtrude","SWEPT_EDGE",EDGE,{"disambiguationData":[OSD([subQ1,subQ0]),TDD([makeQuery(id+"F5.imprint","INTERSECT",VERTEX,{"disambiguationData":[OD(0.0)],"derivedFrom":[subQ1,subQ0]})])]});}
            var Q7;
            Q7=makeQuery(id+"F6.opExtrude","SWEPT_EDGE",EDGE,{"disambiguationData":[OSD([sQuery(id+"F2.wireOp",EDGE,"E76"),sQuery(id+"F5.wireOp",EDGE,"E111")])]});
            var Q8;
            Q8=makeQuery(id+"F6.opExtrude","SWEPT_EDGE",EDGE,{"disambiguationData":[OSD([sQuery(id+"F2.wireOp",EDGE,"E85.trimOffspring"),sQuery(id+"F5.wireOp",EDGE,"E119")])]});
            var Q9;
            {var subQ0=sQuery(id+"F5.wireOp",EDGE,"E119");var subQ1=sQuery(id+"F5.wireOp",EDGE,"E111");Q9=makeQuery(id+"F6.opExtrude","SWEPT_EDGE",EDGE,{"disambiguationData":[OSD([subQ1,subQ0]),TDD([makeQuery(id+"F5.imprint","INTERSECT",VERTEX,{"disambiguationData":[OD(1.0)],"derivedFrom":[subQ1,subQ0]})])]});}
            var Q10;
            Q10=makeQuery(id+"F6.opExtrude","SWEPT_EDGE",EDGE,{"disambiguationData":[OSD([sQuery(id+"F2.wireOp",EDGE,"E81"),sQuery(id+"F5.wireOp",EDGE,"E111")])]});
            var Q11;
            Q11=makeQuery(id+"F6.opExtrude","SWEPT_EDGE",EDGE,{"disambiguationData":[OSD([sQuery(id+"F2.wireOp",EDGE,"E76"),sQuery(id+"F5.wireOp",EDGE,"E120")])]});
            var Q12;
            Q12=makeQuery(id+"F6.opExtrude","SWEPT_EDGE",EDGE,{"disambiguationData":[OSD([sQuery(id+"F5.wireOp",EDGE,"E112"),sQuery(id+"F5.wireOp",EDGE,"E120")])]});
            var Q13;
            Q13=makeQuery(id+"F6.opExtrude","SWEPT_EDGE",EDGE,{"disambiguationData":[OSD([sQuery(id+"F2.wireOp",EDGE,"E75"),sQuery(id+"F5.wireOp",EDGE,"E112")])]});
            var Q14;
            {var subQ0=sQuery(id+"F5.wireOp",EDGE,"E112");var subQ1=sQuery(id+"F2.wireOp",EDGE,"E82.trimOffspring");Q14=makeQuery(id+"F6.opExtrude","SWEPT_EDGE",EDGE,{"disambiguationData":[OSD([subQ1,subQ0]),TDD([makeQuery(id+"F5.imprint","INTERSECT",VERTEX,{"disambiguationData":[OD(1.0)],"derivedFrom":[makeQuery(id+"F4.opExtrude","CAP_EDGE",EDGE,{"disambiguationData":[OSD([subQ1])],"isStart":false}),subQ0]})])]});}
            var Q15;
            {var subQ0=sQuery(id+"F5.wireOp",EDGE,"E112");var subQ1=sQuery(id+"F2.wireOp",EDGE,"E82.trimOffspring");Q15=makeQuery(id+"F6.opExtrude","SWEPT_EDGE",EDGE,{"disambiguationData":[OSD([subQ1,subQ0]),TDD([makeQuery(id+"F5.imprint","INTERSECT",VERTEX,{"disambiguationData":[OD(0.0)],"derivedFrom":[makeQuery(id+"F4.opExtrude","CAP_EDGE",EDGE,{"disambiguationData":[OSD([subQ1])],"isStart":false}),subQ0]})])]});}
            var Q16;
            Q16=makeQuery(id+"F6.opExtrude","SWEPT_EDGE",EDGE,{"disambiguationData":[OSD([sQuery(id+"F2.wireOp",EDGE,"E59"),sQuery(id+"F5.wireOp",EDGE,"E113")])]});
            var Q17;
            Q17=makeQuery(id+"F6.opExtrude","SWEPT_EDGE",EDGE,{"disambiguationData":[OSD([sQuery(id+"F2.wireOp",EDGE,"E72"),sQuery(id+"F5.wireOp",EDGE,"E113")])]});
            var Q18;
            {var subQ0=sQuery(id+"F5.wireOp",EDGE,"E116");var subQ1=sQuery(id+"F5.wireOp",EDGE,"E108");Q18=makeQuery(id+"F6.opExtrude","SWEPT_EDGE",EDGE,{"disambiguationData":[OSD([subQ1,subQ0]),TDD([makeQuery(id+"F5.imprint","INTERSECT",VERTEX,{"disambiguationData":[OD(0.0)],"derivedFrom":[subQ1,subQ0]})])]});}
            var Q19;
            Q19=makeQuery(id+"F6.opExtrude","SWEPT_EDGE",EDGE,{"disambiguationData":[OSD([sQuery(id+"F2.wireOp",EDGE,"E73"),sQuery(id+"F5.wireOp",EDGE,"E108")])]});
            var Q20;
            Q20=makeQuery(id+"F6.opExtrude","SWEPT_EDGE",EDGE,{"disambiguationData":[OSD([sQuery(id+"F2.wireOp",EDGE,"E98.filletArc"),sQuery(id+"F5.wireOp",EDGE,"E116")])]});
            var Q21;
            Q21=makeQuery(id+"F6.opExtrude","SWEPT_EDGE",EDGE,{"disambiguationData":[OSD([sQuery(id+"F2.wireOp",EDGE,"E97.filletArc"),sQuery(id+"F5.wireOp",EDGE,"E116")])]});
            var Q22;
            {var subQ0=sQuery(id+"F5.wireOp",EDGE,"E116");var subQ1=sQuery(id+"F5.wireOp",EDGE,"E108");Q22=makeQuery(id+"F6.opExtrude","SWEPT_EDGE",EDGE,{"disambiguationData":[OSD([subQ1,subQ0]),TDD([makeQuery(id+"F5.imprint","INTERSECT",VERTEX,{"disambiguationData":[OD(1.0)],"derivedFrom":[subQ1,subQ0]})])]});}
            var Q23;
            Q23=makeQuery(id+"F6.opExtrude","SWEPT_EDGE",EDGE,{"disambiguationData":[OSD([sQuery(id+"F2.wireOp",EDGE,"E78"),sQuery(id+"F5.wireOp",EDGE,"E108")])]});
            fillet(context, id + "F8", {"entities" : qUnion([Q0, Q1, Q2, Q3, Q4, Q5, Q6, Q7, Q8, Q9, Q10, Q11, Q12, Q13, Q14, Q15, Q16, Q17, Q18, Q19, Q20, Q21, Q22, Q23]), "radius" : 5.08 * mm, "tangentPropagation" : true, "allowEdgeOverflow" : false});
        }
    });
